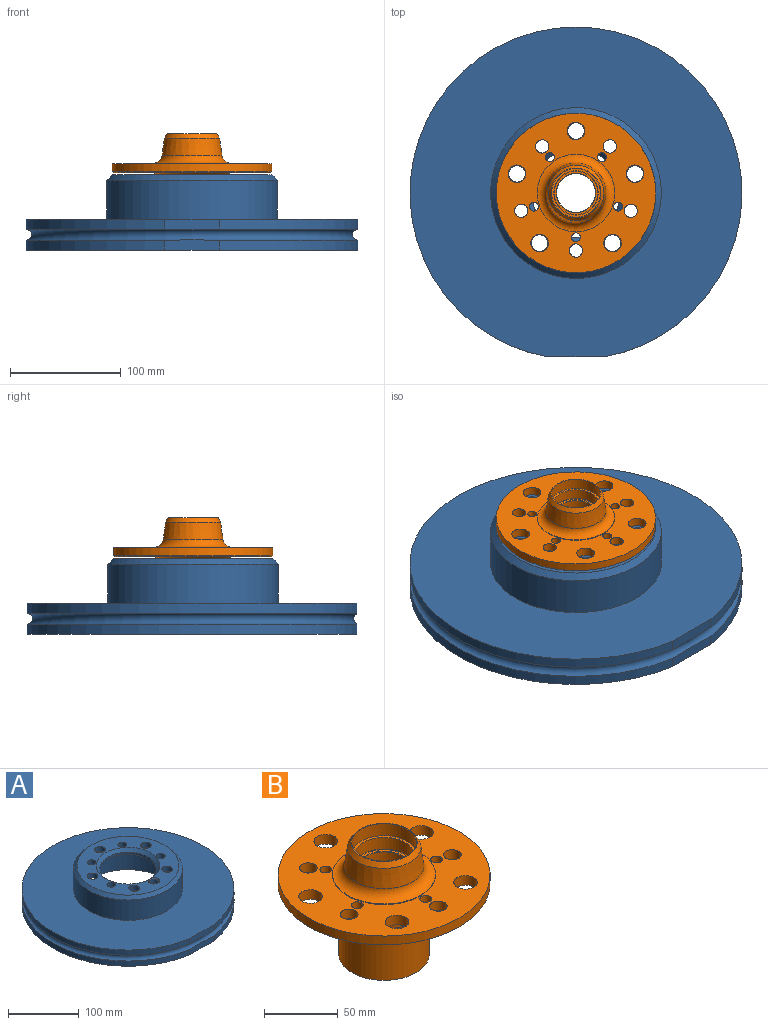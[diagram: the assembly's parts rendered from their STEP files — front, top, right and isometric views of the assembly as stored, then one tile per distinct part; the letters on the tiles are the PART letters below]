
ASSEMBLY  parts=2 mates=1
PART A: 27 faces, bbox 332.4x332.4x68.2 mm
  f0: cylinder r=150mm len=300mm, axis (0,0,-1), area 8040.9mm2, adj f3,f4,f26
  f1: cylinder r=150mm len=300mm, axis (0,0,-1), area 8040.9mm2, adj f2,f4,f25
  f2: plane 300x298mm, normal (0,0,1), area 51945.7mm2, adj f1,f6,f25
  f3: plane 300x298mm, normal (0,0,-1), area 45596.1mm2, adj f0,f11,f26
  f4: torus R=150mm, axis (0,0,-1), area 14357.3mm2, adj f0,f1,f25,f26
  f5: cylinder r=72.5mm len=145mm, axis (0,0,-1), area 22639.9mm2, adj f8,f10
  f6: cylinder r=77.1mm len=154.2mm, axis (0,0,-1), area 17052.1mm2, adj f2,f12
  f7: plane 144.2x144.2mm, normal (0,0,1), area 8417.9mm2, adj f12,f13,f14,f15,f16,f18,f19,f20
  f8: plane 145x145mm, normal (0,0,-1), area 10018.4mm2, adj f5,f9,f14,f15,f16,f17,f18,f19
  f9: cylinder r=40mm len=80mm, axis (0,0,1), area 879.6mm2, adj f8,f13
  f10: plane 178.5x178.5mm, normal (0,0,-1), area 8511.6mm2, adj f5,f11
  f11: cylinder r=89.25mm len=178.5mm, axis (0,0,-1), area 5607.7mm2, adj f3,f10
  f12: cone r=72.1mm half-angle=45deg, axis (0,0,-1), area 3314.4mm2, adj f6,f7
  f13: cone r=40mm half-angle=45deg, axis (0,0,1), area 1884.3mm2, adj f7,f9,f24
  f14: cylinder r=6.1mm len=12.2mm, axis (0,0,1), area 325.8mm2, adj f7,f8
  f15: cylinder r=6.1mm len=12.2mm, axis (0,0,1), area 325.8mm2, adj f7,f8
  f16: cylinder r=6.1mm len=12.2mm, axis (0,0,1), area 325.8mm2, adj f7,f8
  f17: cylinder r=6.1mm len=12.2mm, axis (0,0,1), area 249.1mm2, adj f8,f24
  f18: cylinder r=7.5mm len=15mm, axis (0,0,1), area 400.6mm2, adj f7,f8
  f19: cylinder r=7.5mm len=15mm, axis (0,0,1), area 400.6mm2, adj f7,f8
  f20: cylinder r=7.5mm len=15mm, axis (0,0,1), area 400.6mm2, adj f7,f8
  f21: cylinder r=7.5mm len=15mm, axis (0,0,1), area 400.6mm2, adj f7,f8
  f22: cylinder r=6.1mm len=12.2mm, axis (0,0,1), area 325.8mm2, adj f7,f8
  f23: cylinder r=7.5mm len=15mm, axis (0,0,1), area 400.6mm2, adj f7,f8
  f24: cone r=6.1mm half-angle=45deg, axis (0,0,1), area 122.2mm2, adj f7,f13,f17
  f25: plane 48.83x9.42mm, normal (0,-1,0), area 450.2mm2, adj f1,f2,f4
  f26: plane 48.83x9.42mm, normal (0,-1,0), area 450.2mm2, adj f0,f3,f4
PART B: 46 faces, bbox 144x144x93 mm
  f0: cylinder r=20mm len=40mm, axis (0,0,1), area 1218.9mm2, adj f38,f44
  f1: cone r=77mm half-angle=56.3deg, axis (0,0,1), area 539.9mm2, adj f37,f42
  f2: cylinder r=4mm len=8mm, axis (0,0,1), area 201.1mm2, adj f17,f42
  f3: cylinder r=4mm len=8mm, axis (0,0,1), area 201.1mm2, adj f17,f42
  f4: cylinder r=4mm len=8mm, axis (0,0,1), area 201.1mm2, adj f17,f42
  f5: cylinder r=4mm len=8mm, axis (0,0,1), area 201.1mm2, adj f17,f42
  f6: cylinder r=4mm len=8mm, axis (0,0,1), area 201.1mm2, adj f17,f42
  f7: cylinder r=8mm len=16mm, axis (0,0,1), area 402.1mm2, adj f17,f42
  f8: cylinder r=8mm len=16mm, axis (0,0,1), area 402.1mm2, adj f17,f42
  f9: cylinder r=8mm len=16mm, axis (0,0,1), area 402.1mm2, adj f17,f42
  f10: cylinder r=8mm len=16mm, axis (0,0,1), area 402.1mm2, adj f17,f42
  f11: cylinder r=8mm len=16mm, axis (0,0,1), area 402.1mm2, adj f17,f42
  f12: cylinder r=6mm len=12mm, axis (0,0,1), area 301.6mm2, adj f17,f42
  f13: cylinder r=6mm len=12mm, axis (0,0,1), area 301.6mm2, adj f17,f42
  f14: cylinder r=6mm len=12mm, axis (0,0,1), area 301.6mm2, adj f17,f42
  f15: cylinder r=6mm len=12mm, axis (0,0,1), area 301.6mm2, adj f17,f42
  f16: cylinder r=6mm len=12mm, axis (0,0,1), area 301.6mm2, adj f17,f42
  f17: plane 144x144mm, normal (0,0,1), area 10615.4mm2, adj f2,f3,f4,f5,f6,f7,f8,f9
  f18: cylinder r=17.5mm len=35mm, axis (0,0,1), area 1143.5mm2, adj f39,f40
  f19: plane 61.4x61.4mm, normal (0,0,-1), area 133.5mm2, adj f20,f36
  f20: cylinder r=30.7mm len=61.4mm, axis (0,0,1), area 8294.4mm2, adj f19,f21
  f21: plane 62x62mm, normal (0,0,-1), area 58.2mm2, adj f20,f22
  f22: cylinder r=31mm len=62mm, axis (0,0,1), area 1947.8mm2, adj f21,f43
  f23: cylinder r=35mm len=70mm, axis (0,0,1), area 110mm2, adj f17,f24
  f24: torus R=35mm, axis (0,0,1), area 2202mm2, adj f23,f25
  f25: cone r=25mm half-angle=7.4deg, axis (0,0,-1), area 2547.9mm2, adj f24,f26
  f26: cone r=22.5mm half-angle=32deg, axis (0,0,-1), area 703.9mm2, adj f25,f27
  f27: plane 45x45mm, normal (0,0,1), area 69.9mm2, adj f26,f35
  f28: plane 39.4x39.4mm, normal (0,0,1), area 223.8mm2, adj f38,f39
  f29: plane 58x58mm, normal (0,0,-1), area 678.6mm2, adj f30,f32
  f30: cylinder r=29mm len=58mm, axis (0,0,-1), area 1731mm2, adj f29,f36
  f31: plane 50x50mm, normal (0,0,-1), area 373.1mm2, adj f32,f34
  f32: cylinder r=25mm len=50mm, axis (0,0,-1), area 1727.9mm2, adj f29,f31
  f33: plane 44.4x44.4mm, normal (0,0,-1), area 552.9mm2, adj f40,f41
  f34: cylinder r=22.5mm len=45mm, axis (0,0,-1), area 5753.8mm2, adj f31,f41
  f35: cone r=20mm half-angle=45deg, axis (0,0,1), area 2mm2, adj f27,f45
  f36: cone r=29mm half-angle=63.4deg, axis (0,0,-1), area 207.2mm2, adj f19,f30
  f37: cylinder r=72mm len=144mm, axis (0,0,1), area 3317.5mm2, adj f1,f17
  f38: cone r=19.7mm half-angle=45deg, axis (0,0,1), area 52.9mm2, adj f0,f28
  f39: cone r=17.5mm half-angle=45deg, axis (0,0,1), area 47.1mm2, adj f18,f28
  f40: cone r=17.8mm half-angle=45deg, axis (0,0,-1), area 47.1mm2, adj f18,f33
  f41: cone r=22.2mm half-angle=45deg, axis (0,0,-1), area 59.6mm2, adj f33,f34
  f42: plane 142x142mm, normal (0,0,-1), area 9943.1mm2, adj f1,f2,f3,f4,f5,f6,f7,f8
  f43: torus R=36mm, axis (0,0,-1), area 1619.4mm2, adj f22,f42
  f44: plane 43.98x43.98mm, normal (0,0,1), area 262.5mm2, adj f0,f45
  f45: cylinder r=21.99mm len=43.98mm, axis (0,0,1), area 1380.3mm2, adj f35,f44
PLACE A t=(0,0,-68.2)mm
PLACE B at identity fixed
MATE slider A.f9 <-> B.f20  axis (0,0,1) through (0,0,-5)mm
